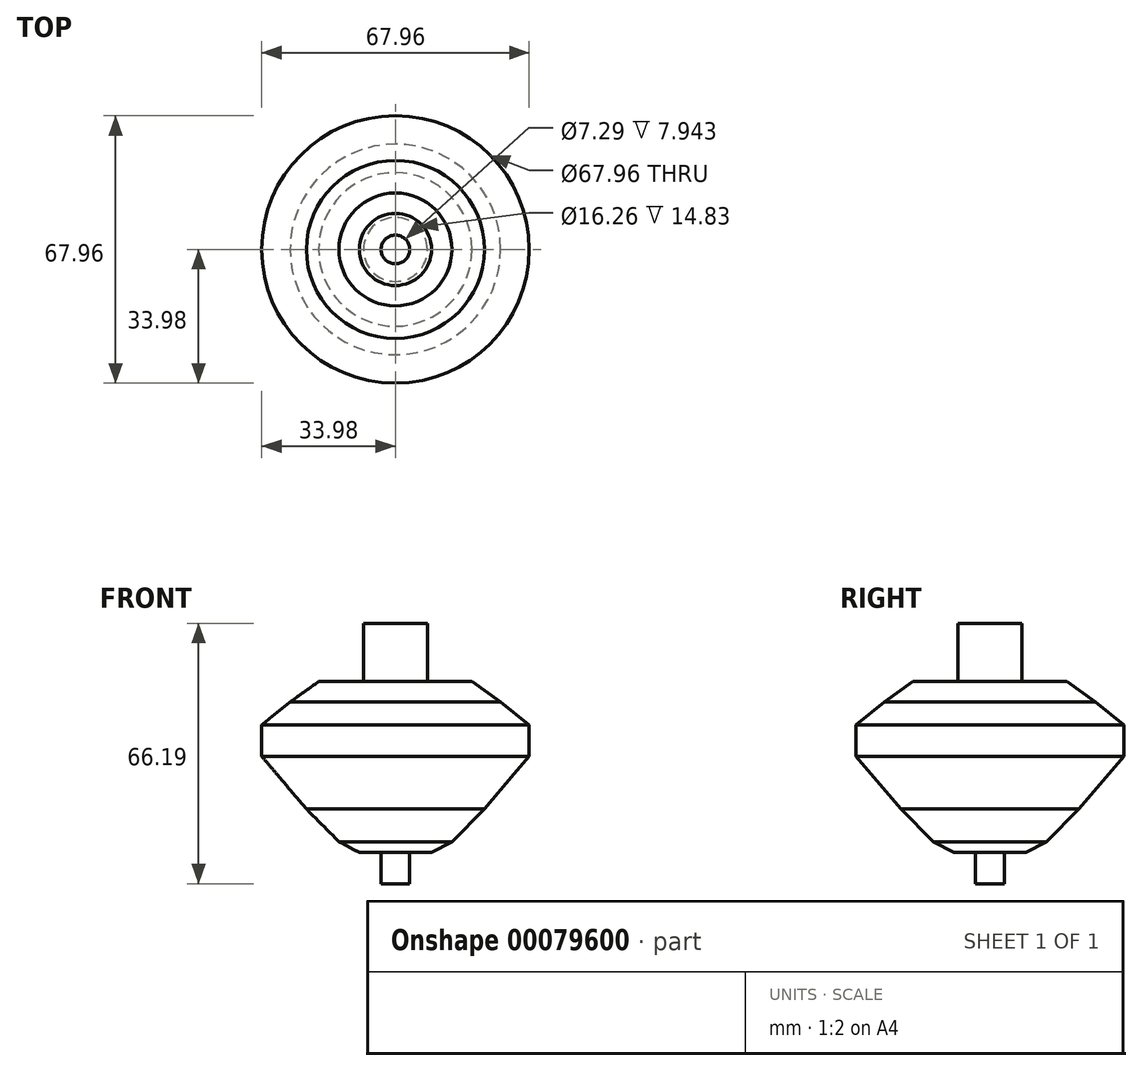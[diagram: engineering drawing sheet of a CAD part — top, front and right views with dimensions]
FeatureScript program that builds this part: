
annotation { "Feature Type Name" : "Feature", "Feature Type Description" : "" }
export const myFeature = defineFeature(function(context is Context, id is Id, definition is map)
    precondition{}
    {
        {
            var Q0;
            Q0=qCreatedBy(makeId("Front.planeOp"),FACE);
            var sketch = newSketch(context, id + "F0", { "sketchPlane" : qUnion([Q0])});
            skLineSegment(sketch, "E0", {"start": v(0, 14.83) * mm, "end": v(-8.13, 14.83) * mm});
            skLineSegment(sketch, "E1", {"start": v(-8.13, 14.83) * mm, "end": v(-8.13, 0) * mm});
            skLineSegment(sketch, "E2", {"start": v(-8.13, 0) * mm, "end": v(-19.5, 0) * mm});
            skLineSegment(sketch, "E3", {"start": v(-19.5, 0) * mm, "end": v(-26.74, -5.16) * mm});
            skLineSegment(sketch, "E4", {"start": v(-26.74, -5.16) * mm, "end": v(-33.98, -11.02) * mm});
            skLineSegment(sketch, "E5", {"start": v(-33.98, -11.02) * mm, "end": v(-33.98, -18.95) * mm});
            skLineSegment(sketch, "E6", {"start": v(-33.98, -18.95) * mm, "end": v(-30.19, -23.43) * mm});
            skLineSegment(sketch, "E7", {"start": v(-30.19, -23.43) * mm, "end": v(-22.6, -32.4) * mm});
            skLineSegment(sketch, "E8", {"start": v(-22.6, -32.4) * mm, "end": v(-14.33, -40.66) * mm});
            skLineSegment(sketch, "E9", {"start": v(-14.33, -40.66) * mm, "end": v(-9.16, -43.42) * mm});
            skLineSegment(sketch, "E10", {"start": v(-9.16, -43.42) * mm, "end": v(-3.65, -43.42) * mm});
            skLineSegment(sketch, "E11", {"start": v(-3.65, -43.42) * mm, "end": v(-3.65, -51.36) * mm});
            skLineSegment(sketch, "E12", {"start": v(-3.65, -51.36) * mm, "end": v(0, -51.36) * mm});
            skLineSegment(sketch, "E13", {"start": v(0, 14.83) * mm, "end": v(0, -51.36) * mm});
            skSolve(sketch);
        }
        {
            var Q0;
            Q0=sQuery(id+"F0.wireOp",EDGE,"E1");
            var Q1;
            Q1=sQuery(id+"F0.wireOp",EDGE,"E0");
            var Q2;
            Q2=sQuery(id+"F0.wireOp",EDGE,"E2");
            var Q3;
            Q3=sQuery(id+"F0.wireOp",EDGE,"E3");
            var Q4;
            Q4=sQuery(id+"F0.wireOp",EDGE,"E4");
            var Q5;
            Q5=sQuery(id+"F0.wireOp",EDGE,"E5");
            var Q6;
            Q6=sQuery(id+"F0.wireOp",EDGE,"E6");
            var Q7;
            Q7=sQuery(id+"F0.wireOp",EDGE,"E7");
            var Q8;
            Q8=sQuery(id+"F0.wireOp",EDGE,"E8");
            var Q9;
            Q9=sQuery(id+"F0.wireOp",EDGE,"E9");
            var Q10;
            Q10=sQuery(id+"F0.wireOp",EDGE,"E10");
            var Q11;
            Q11=sQuery(id+"F0.wireOp",EDGE,"E11");
            var Q12;
            Q12=sQuery(id+"F0.wireOp",EDGE,"E12");
            var Q13;
            Q13=sQuery(id+"F0.wireOp",EDGE,"E13");
            revolve(context, id + "F1", {"bodyType" : ToolBodyType.SURFACE, "surfaceEntities" : qUnion([Q0, Q1, Q2, Q3, Q4, Q5, Q6, Q7, Q8, Q9, Q10, Q11, Q12]), "axis" : qUnion([Q13]), "revolveType" : RevolveType.FULL});
        }
    });
